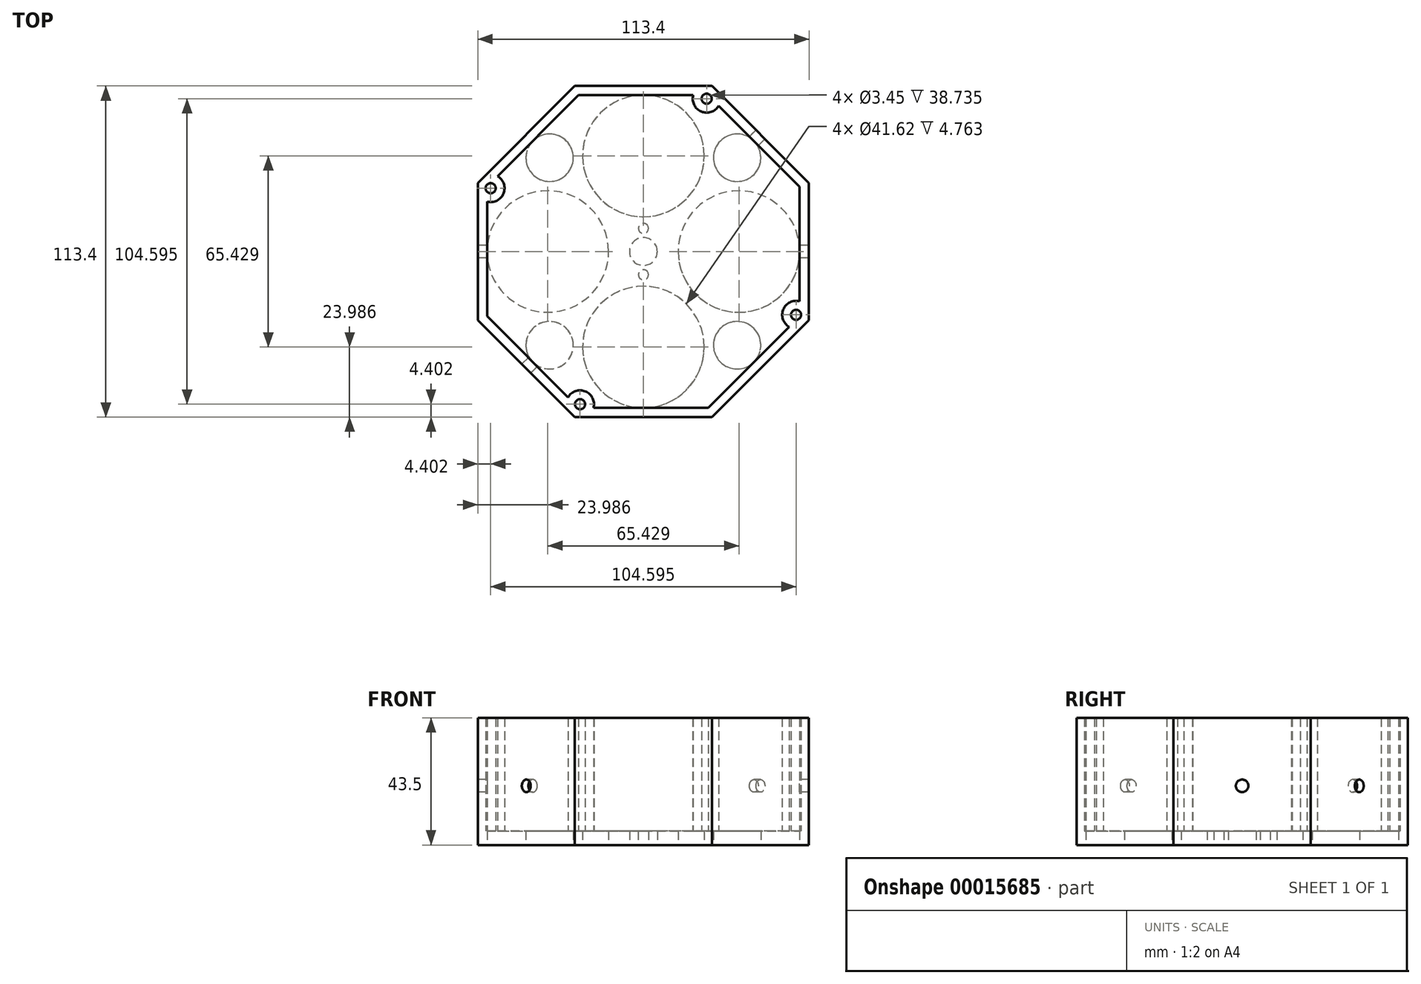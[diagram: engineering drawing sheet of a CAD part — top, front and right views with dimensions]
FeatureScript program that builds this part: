
annotation { "Feature Type Name" : "Feature", "Feature Type Description" : "" }
export const myFeature = defineFeature(function(context is Context, id is Id, definition is map)
    precondition{}
    {
        {
            var Q0;
            Q0=qCreatedBy(makeId("Top.planeOp"),FACE);
            var sketch = newSketch(context, id + "F0", { "sketchPlane" : qUnion([Q0])});
            skCircle(sketch, "E0.cCircle", {"center": v(0, 0) * mm, "radius": 56.7 * mm, "construction": true});
            skLineSegment(sketch, "E0.0", {"start": v(56.7, 23.48) * mm, "end": v(56.7, -23.48) * mm});
            skLineSegment(sketch, "E0.1", {"start": v(56.7, -23.48) * mm, "end": v(23.48, -56.7) * mm});
            skLineSegment(sketch, "E0.2", {"start": v(23.48, -56.7) * mm, "end": v(-23.48, -56.7) * mm});
            skLineSegment(sketch, "E0.3", {"start": v(-23.48, -56.7) * mm, "end": v(-56.7, -23.48) * mm});
            skLineSegment(sketch, "E0.4", {"start": v(-56.7, -23.48) * mm, "end": v(-56.7, 23.48) * mm});
            skLineSegment(sketch, "E0.5", {"start": v(-56.7, 23.48) * mm, "end": v(-23.48, 56.7) * mm});
            skLineSegment(sketch, "E0.6", {"start": v(-23.48, 56.7) * mm, "end": v(23.48, 56.7) * mm});
            skLineSegment(sketch, "E0.7", {"start": v(23.48, 56.7) * mm, "end": v(56.7, 23.48) * mm});
            skPoint(sketch, "E0.0.midPoint", {"position": v(56.7, 0) * mm});
            skCircle(sketch, "E1", {"center": v(0, -7.94) * mm, "radius": 1.73 * mm});
            skCircle(sketch, "E2", {"center": v(0, 0) * mm, "radius": 4.76 * mm});
            skCircle(sketch, "E3", {"center": v(0, 7.94) * mm, "radius": 1.73 * mm});
            skLineSegment(sketch, "E4", {"start": v(0, -7.94) * mm, "end": v(0, 7.94) * mm});
            skSolve(sketch);
        }
        {
            var Q0;
            Q0 = qSketchRegion(id + "F0", true);
            extrude(context, id + "F1", {"entities" : qUnion([Q0]), "depth" : 4.76 * mm});
        }
        {
            var Q0;
            Q0=makeQuery(id+"F1.opExtrude","CAP_FACE",FACE,{"disambiguationData":[OSD([sQuery(id+"F0.wireOp",EDGE,"E0.0"),sQuery(id+"F0.wireOp",EDGE,"E0.1"),sQuery(id+"F0.wireOp",EDGE,"E0.2"),sQuery(id+"F0.wireOp",EDGE,"E0.3"),sQuery(id+"F0.wireOp",EDGE,"E0.4"),sQuery(id+"F0.wireOp",EDGE,"E0.5"),sQuery(id+"F0.wireOp",EDGE,"E0.6"),sQuery(id+"F0.wireOp",EDGE,"E0.7")])],"isStart":false});
            var sketch = newSketch(context, id + "F2", { "sketchPlane" : qUnion([Q0])});
            skCircle(sketch, "E5.cCircle", {"center": v(0, 0) * mm, "radius": 53.52 * mm, "construction": true});
            skLineSegment(sketch, "E5.0", {"start": v(-22.17, 53.52) * mm, "end": v(22.17, 53.52) * mm});
            skLineSegment(sketch, "E5.1", {"start": v(22.17, 53.52) * mm, "end": v(53.52, 22.17) * mm});
            skLineSegment(sketch, "E5.2", {"start": v(53.52, 22.17) * mm, "end": v(53.52, -22.17) * mm});
            skLineSegment(sketch, "E5.3", {"start": v(53.52, -22.17) * mm, "end": v(22.17, -53.52) * mm});
            skLineSegment(sketch, "E5.4", {"start": v(22.17, -53.52) * mm, "end": v(-22.17, -53.52) * mm});
            skLineSegment(sketch, "E5.5", {"start": v(-22.17, -53.52) * mm, "end": v(-53.52, -22.17) * mm});
            skLineSegment(sketch, "E5.6", {"start": v(-53.52, -22.17) * mm, "end": v(-53.52, 22.17) * mm});
            skLineSegment(sketch, "E5.7", {"start": v(-53.52, 22.17) * mm, "end": v(-22.17, 53.52) * mm});
            skPoint(sketch, "E5.0.midPoint", {"position": v(0, 53.52) * mm});
            skCircle(sketch, "E6.cCircle", {"center": v(0, 0) * mm, "radius": 56.7 * mm, "construction": true});
            skLineSegment(sketch, "E6.0", {"start": v(-23.48, 56.7) * mm, "end": v(23.48, 56.7) * mm});
            skLineSegment(sketch, "E6.1", {"start": v(23.48, 56.7) * mm, "end": v(56.7, 23.48) * mm});
            skLineSegment(sketch, "E6.2", {"start": v(56.7, 23.48) * mm, "end": v(56.7, -23.48) * mm});
            skLineSegment(sketch, "E6.3", {"start": v(56.7, -23.48) * mm, "end": v(23.48, -56.7) * mm});
            skLineSegment(sketch, "E6.4", {"start": v(23.48, -56.7) * mm, "end": v(-23.48, -56.7) * mm});
            skLineSegment(sketch, "E6.5", {"start": v(-23.48, -56.7) * mm, "end": v(-56.7, -23.48) * mm});
            skLineSegment(sketch, "E6.6", {"start": v(-56.7, -23.48) * mm, "end": v(-56.7, 23.48) * mm});
            skLineSegment(sketch, "E6.7", {"start": v(-56.7, 23.48) * mm, "end": v(-23.48, 56.7) * mm});
            skPoint(sketch, "E6.0.midPoint", {"position": v(0, 56.7) * mm});
            skLineSegment(sketch, "E7", {"start": v(0, 56.7) * mm, "end": v(0, 53.52) * mm});
            skLineSegment(sketch, "E8", {"start": v(22.17, 53.52) * mm, "end": v(21.66, 52.3) * mm, "construction": true});
            skLineSegment(sketch, "E9", {"start": v(21.66, 52.3) * mm, "end": v(0, 0) * mm, "construction": true});
            skLineSegment(sketch, "E10", {"start": v(0, 0) * mm, "end": v(-52.3, 21.66) * mm, "construction": true});
            skLineSegment(sketch, "E11", {"start": v(-52.3, 21.66) * mm, "end": v(-53.52, 22.17) * mm, "construction": true});
            skLineSegment(sketch, "E12", {"start": v(0, 0) * mm, "end": v(52.3, -21.66) * mm, "construction": true});
            skLineSegment(sketch, "E13", {"start": v(52.3, -21.66) * mm, "end": v(53.52, -22.17) * mm, "construction": true});
            skLineSegment(sketch, "E14", {"start": v(0, 0) * mm, "end": v(-21.66, -52.3) * mm, "construction": true});
            skLineSegment(sketch, "E15", {"start": v(-21.66, -52.3) * mm, "end": v(-22.17, -53.52) * mm, "construction": true});
            skLineSegment(sketch, "E16", {"start": v(26.06, 50.48) * mm, "end": v(17.26, 54.12) * mm, "construction": true});
            skLineSegment(sketch, "E17", {"start": v(17.01, 53.52) * mm, "end": v(17.26, 54.12) * mm, "construction": true});
            skLineSegment(sketch, "E18", {"start": v(25.81, 49.88) * mm, "end": v(26.06, 50.48) * mm, "construction": true});
            skArc(sketch, "E19", {"start": v(17.26, 54.12) * mm, "mid": v(19.84, 47.9) * mm, "end": v(26.06, 50.48) * mm});
            skCircle(sketch, "E20", {"center": v(21.66, 52.3) * mm, "radius": 1.73 * mm});
            skLineSegment(sketch, "E21", {"start": v(-50.48, 26.06) * mm, "end": v(-54.12, 17.26) * mm, "construction": true});
            skArc(sketch, "E22", {"start": v(-54.12, 17.26) * mm, "mid": v(-47.9, 19.84) * mm, "end": v(-50.48, 26.06) * mm});
            skCircle(sketch, "E23", {"center": v(-52.3, 21.66) * mm, "radius": 1.73 * mm});
            skLineSegment(sketch, "E24", {"start": v(54.12, -17.26) * mm, "end": v(50.48, -26.06) * mm, "construction": true});
            skLineSegment(sketch, "E25", {"start": v(-17.26, -54.12) * mm, "end": v(-26.06, -50.48) * mm, "construction": true});
            skArc(sketch, "E26", {"start": v(54.12, -17.26) * mm, "mid": v(47.9, -19.84) * mm, "end": v(50.48, -26.06) * mm});
            skArc(sketch, "E27", {"start": v(-17.26, -54.12) * mm, "mid": v(-19.84, -47.9) * mm, "end": v(-26.06, -50.48) * mm});
            skCircle(sketch, "E28", {"center": v(52.3, -21.66) * mm, "radius": 1.73 * mm});
            skCircle(sketch, "E29", {"center": v(-21.66, -52.3) * mm, "radius": 1.73 * mm});
            skSolve(sketch);
        }
        {
            var Q0;
            Q0 = qSketchRegion(id + "F2", true);
            var Q1;
            {var subQ3=sQuery(id+"F2.wireOp",EDGE,"E5.0");var subQ5=sQuery(id+"F2.wireOp",EDGE,"E19");var subQ7=makeQuery(id+"F2.imprint","INTERSECT",VERTEX,{"derivedFrom":[subQ3,subQ5]});Q1=makeQuery(id+"F2.imprint","IMPRINT",FACE,{"disambiguationData":[TD([[makeQuery(id+"F2.imprint","IMPRINT",EDGE,{"disambiguationData":[TD([[subQ7,-1.0]])],"derivedFrom":subQ3}),-1.0]])]});}
            var Q2;
            {var subQ3=sQuery(id+"F2.wireOp",EDGE,"E5.2");var subQ5=sQuery(id+"F2.wireOp",EDGE,"E26");var subQ7=makeQuery(id+"F2.imprint","INTERSECT",VERTEX,{"derivedFrom":[subQ3,subQ5]});Q2=makeQuery(id+"F2.imprint","IMPRINT",FACE,{"disambiguationData":[TD([[makeQuery(id+"F2.imprint","IMPRINT",EDGE,{"disambiguationData":[TD([[subQ7,-1.0]])],"derivedFrom":subQ3}),-1.0]])]});}
            var Q3;
            {var subQ3=sQuery(id+"F2.wireOp",EDGE,"E5.4");var subQ5=sQuery(id+"F2.wireOp",EDGE,"E27");var subQ7=makeQuery(id+"F2.imprint","INTERSECT",VERTEX,{"derivedFrom":[subQ3,subQ5]});Q3=makeQuery(id+"F2.imprint","IMPRINT",FACE,{"disambiguationData":[TD([[makeQuery(id+"F2.imprint","IMPRINT",EDGE,{"disambiguationData":[TD([[subQ7,-1.0]])],"derivedFrom":subQ3}),-1.0]])]});}
            var Q4;
            {var subQ3=sQuery(id+"F2.wireOp",EDGE,"E5.6");var subQ5=sQuery(id+"F2.wireOp",EDGE,"E22");var subQ7=makeQuery(id+"F2.imprint","INTERSECT",VERTEX,{"derivedFrom":[subQ3,subQ5]});Q4=makeQuery(id+"F2.imprint","IMPRINT",FACE,{"disambiguationData":[TD([[makeQuery(id+"F2.imprint","IMPRINT",EDGE,{"disambiguationData":[TD([[subQ7,-1.0]])],"derivedFrom":subQ3}),-1.0]])]});}
            extrude(context, id + "F3", {"entities" : qUnion([Q0, Q1, Q2, Q3, Q4]), "operationType" : NewBodyOperationType.ADD, "depth" : 38.73 * mm});
        }
        {
            var Q0;
            Q0=makeQuery(id+"F3.boolean.opBoolean","MERGE",FACE,{"derivedFrom":[makeQuery(id+"F1.opExtrude","SWEPT_FACE",FACE,{"disambiguationData":[OSD([sQuery(id+"F0.wireOp",EDGE,"E0.4")])]}),makeQuery(id+"F3.opExtrude","SWEPT_FACE",FACE,{"disambiguationData":[OSD([sQuery(id+"F2.wireOp",EDGE,"E6.6")])]})]});
            var sketch = newSketch(context, id + "F4", { "sketchPlane" : qUnion([Q0])});
            skLineSegment(sketch, "E30", {"start": v(0, 0) * mm, "end": v(0, 20.24) * mm});
            skCircle(sketch, "E31", {"center": v(0, 20.24) * mm, "radius": 2.16 * mm});
            skSolve(sketch);
        }
        {
            var Q0;
            Q0 = qSketchRegion(id + "F4", true);
            var Q1;
            Q1=makeQuery(id+"F3.boolean.opBoolean","MERGE",FACE,{"derivedFrom":[makeQuery(id+"F1.opExtrude","SWEPT_FACE",FACE,{"disambiguationData":[OSD([sQuery(id+"F0.wireOp",EDGE,"E0.0")])]}),makeQuery(id+"F3.opExtrude","SWEPT_FACE",FACE,{"disambiguationData":[OSD([sQuery(id+"F2.wireOp",EDGE,"E6.2")])]})]});
            extrude(context, id + "F5", {"entities" : qUnion([Q0]), "operationType" : NewBodyOperationType.REMOVE, "endBound" : BoundingType.UP_TO_SURFACE, "oppositeDirection" : true, "endBoundEntityFace" : qUnion([Q1]), "depth" : 25.4 * mm});
        }
        {
            var Q0;
            Q0=makeQuery(id+"F3.boolean.opBoolean","MERGE",FACE,{"derivedFrom":[makeQuery(id+"F1.opExtrude","SWEPT_FACE",FACE,{"disambiguationData":[OSD([sQuery(id+"F0.wireOp",EDGE,"E0.3")])]}),makeQuery(id+"F3.opExtrude","SWEPT_FACE",FACE,{"disambiguationData":[OSD([sQuery(id+"F2.wireOp",EDGE,"E6.5")])]})]});
            var sketch = newSketch(context, id + "F6", { "sketchPlane" : qUnion([Q0])});
            skLineSegment(sketch, "E32", {"start": v(0, 0) * mm, "end": v(0, 20.24) * mm});
            skCircle(sketch, "E33", {"center": v(0, 20.24) * mm, "radius": 2.16 * mm});
            skSolve(sketch);
        }
        {
            var Q0;
            Q0 = qSketchRegion(id + "F6", true);
            var Q1;
            Q1=makeQuery(id+"F3.boolean.opBoolean","MERGE",FACE,{"derivedFrom":[makeQuery(id+"F1.opExtrude","SWEPT_FACE",FACE,{"disambiguationData":[OSD([sQuery(id+"F0.wireOp",EDGE,"E0.7")])]}),makeQuery(id+"F3.opExtrude","SWEPT_FACE",FACE,{"disambiguationData":[OSD([sQuery(id+"F2.wireOp",EDGE,"E6.1")])]})]});
            extrude(context, id + "F7", {"entities" : qUnion([Q0]), "operationType" : NewBodyOperationType.REMOVE, "endBound" : BoundingType.UP_TO_SURFACE, "oppositeDirection" : true, "endBoundEntityFace" : qUnion([Q1]), "depth" : 25.4 * mm});
        }
        {
            var Q0;
            Q0=makeQuery(id+"F1.opExtrude","CAP_FACE",FACE,{"disambiguationData":[OSD([sQuery(id+"F0.wireOp",EDGE,"E0.0"),sQuery(id+"F0.wireOp",EDGE,"E0.1"),sQuery(id+"F0.wireOp",EDGE,"E0.2"),sQuery(id+"F0.wireOp",EDGE,"E0.3"),sQuery(id+"F0.wireOp",EDGE,"E0.4"),sQuery(id+"F0.wireOp",EDGE,"E0.5"),sQuery(id+"F0.wireOp",EDGE,"E0.6"),sQuery(id+"F0.wireOp",EDGE,"E0.7"),sQuery(id+"F0.wireOp",EDGE,"E1"),sQuery(id+"F0.wireOp",EDGE,"E2"),sQuery(id+"F0.wireOp",EDGE,"E3")])],"isStart":true});
            var sketch = newSketch(context, id + "F8", { "sketchPlane" : qUnion([Q0])});
            skCircle(sketch, "E34.cCircle", {"center": v(0, 0) * mm, "radius": 32.71 * mm, "construction": true});
            skLineSegment(sketch, "E34.0", {"start": v(-13.55, 32.71) * mm, "end": v(13.55, 32.71) * mm, "construction": true});
            skLineSegment(sketch, "E34.1", {"start": v(13.55, 32.71) * mm, "end": v(32.71, 13.55) * mm, "construction": true});
            skLineSegment(sketch, "E34.2", {"start": v(32.71, 13.55) * mm, "end": v(32.71, -13.55) * mm, "construction": true});
            skLineSegment(sketch, "E34.3", {"start": v(32.71, -13.55) * mm, "end": v(13.55, -32.71) * mm, "construction": true});
            skLineSegment(sketch, "E34.4", {"start": v(13.55, -32.71) * mm, "end": v(-13.55, -32.71) * mm, "construction": true});
            skLineSegment(sketch, "E34.5", {"start": v(-13.55, -32.71) * mm, "end": v(-32.71, -13.55) * mm, "construction": true});
            skLineSegment(sketch, "E34.6", {"start": v(-32.71, -13.55) * mm, "end": v(-32.71, 13.55) * mm, "construction": true});
            skLineSegment(sketch, "E34.7", {"start": v(-32.71, 13.55) * mm, "end": v(-13.55, 32.71) * mm, "construction": true});
            skPoint(sketch, "E34.0.midPoint", {"position": v(0, 32.71) * mm});
            skCircle(sketch, "E35", {"center": v(0, 32.71) * mm, "radius": 20.8 * mm});
            skCircle(sketch, "E36", {"center": v(32.71, 0) * mm, "radius": 20.8 * mm});
            skCircle(sketch, "E37", {"center": v(0, -32.71) * mm, "radius": 20.8 * mm});
            skCircle(sketch, "E38", {"center": v(-32.71, 0) * mm, "radius": 20.8 * mm});
            skCircle(sketch, "E39", {"center": v(32.1, 32.1) * mm, "radius": 11.3 * mm, "construction": true});
            skCircle(sketch, "E40", {"center": v(32.1, 32.1) * mm, "radius": 8.12 * mm});
            skCircle(sketch, "E41", {"center": v(-32.1, 32.1) * mm, "radius": 11.3 * mm, "construction": true});
            skCircle(sketch, "E42", {"center": v(-32.1, 32.1) * mm, "radius": 8.12 * mm});
            skCircle(sketch, "E43", {"center": v(-32.1, -32.1) * mm, "radius": 11.3 * mm, "construction": true});
            skCircle(sketch, "E44", {"center": v(-32.1, -32.1) * mm, "radius": 8.12 * mm});
            skCircle(sketch, "E45", {"center": v(32.1, -32.1) * mm, "radius": 11.3 * mm, "construction": true});
            skCircle(sketch, "E46", {"center": v(32.1, -32.1) * mm, "radius": 8.12 * mm});
            skLineSegment(sketch, "E47", {"start": v(32.71, 0) * mm, "end": v(56.7, 0) * mm, "construction": true});
            skSolve(sketch);
        }
        {
            var Q0;
            Q0 = qSketchRegion(id + "F8", true);
            var Q1;
            {var subQ0=sQuery(id+"F0.wireOp",EDGE,"E1");var subQ1=sQuery(id+"F0.wireOp",EDGE,"E2");var subQ2=sQuery(id+"F0.wireOp",EDGE,"E3");Q1=makeQuery(id+"F3.boolean.opBoolean","SPLIT",FACE,{"disambiguationData":[TD([makeQuery(id+"F1.opExtrude","SWEPT_FACE",FACE,{"disambiguationData":[OSD([subQ0])]})])],"derivedFrom":makeQuery(id+"F1.opExtrude","CAP_FACE",FACE,{"disambiguationData":[OSD([sQuery(id+"F0.wireOp",EDGE,"E0.0"),sQuery(id+"F0.wireOp",EDGE,"E0.1"),sQuery(id+"F0.wireOp",EDGE,"E0.2"),sQuery(id+"F0.wireOp",EDGE,"E0.3"),sQuery(id+"F0.wireOp",EDGE,"E0.4"),sQuery(id+"F0.wireOp",EDGE,"E0.5"),sQuery(id+"F0.wireOp",EDGE,"E0.6"),sQuery(id+"F0.wireOp",EDGE,"E0.7"),subQ0,subQ1,subQ2])],"isStart":false})});}
            extrude(context, id + "F9", {"entities" : qUnion([Q0]), "operationType" : NewBodyOperationType.REMOVE, "endBound" : BoundingType.UP_TO_SURFACE, "oppositeDirection" : true, "endBoundEntityFace" : qUnion([Q1]), "depth" : 25.4 * mm});
        }
    });
